# Revit family: ADB Fourneaux Gaz L800
name_source: partatom
category: Equipement spécialisé
units: mm (PartAtom-declared; Revit-internal decimal feet)

## family parameters
Basée sur le plan de construction = Non
Conserver l'orientation des annotations = Non
Cote de connecteur circulaire = Utiliser le diamètre
Couper avec des vides une fois chargée = Non
Numéro OmniClass = 23.40.40.14.17.11
Partagée = Non
Repère de localisation dans la pièce = Non
Titre OmniClass = Cookers, Ovens, Stoves
Toujours verticalement = Oui
Type d'élément = Normal

## types (3) — shared parameters
Commentaires du type = Gamme Ambassade - Fourneaux gaz
Diamètre de Raccordement Gaz = 21 mm
Fabricant = Société Industrielle de Lacanche
Pbase = 0 W
Pbase gaz = 17 W
URL = https://www.ambassade-de-bourgogne.com
zero-valued in all types: Elévation par défaut

## per-type parameters (varying)
| type | Bouton 841 P | Description | Modèle | Plaques | Poids net à vide |
| 4 feux vifs - 1 four 620 x 400 - CG 841 P | Oui | Fourneau 4 feux vifs - 1 four gaz 620 x 400 | CG 841 P | CG831P_CG831CF_CG841P_Fourneaux 4-3-2 feux vifs : CG841P | 94.00 kg |
| 2 feux vifs - 1 plaque coup de feu - 1 four 620 X 400 - CG 831 CF | Non | Fourneau 2 feux vifs - 1 plaque coup de feu - 1 four gaz 620 X 400 | CG 831 CF | CG831P_CG831CF_CG841P_Fourneaux 4-3-2 feux vifs : CG831CF | 100.00 kg |
| 3 feux vifs - 1 four 620 x 400 - CG 831 P | Non | Fourneau 3 feux vifs - 1 four gaz 620 x 400 | CG 831 P | CG831P_CG831CF_CG841P_Fourneaux 4-3-2 feux vifs : CG831P | 92.00 kg |
